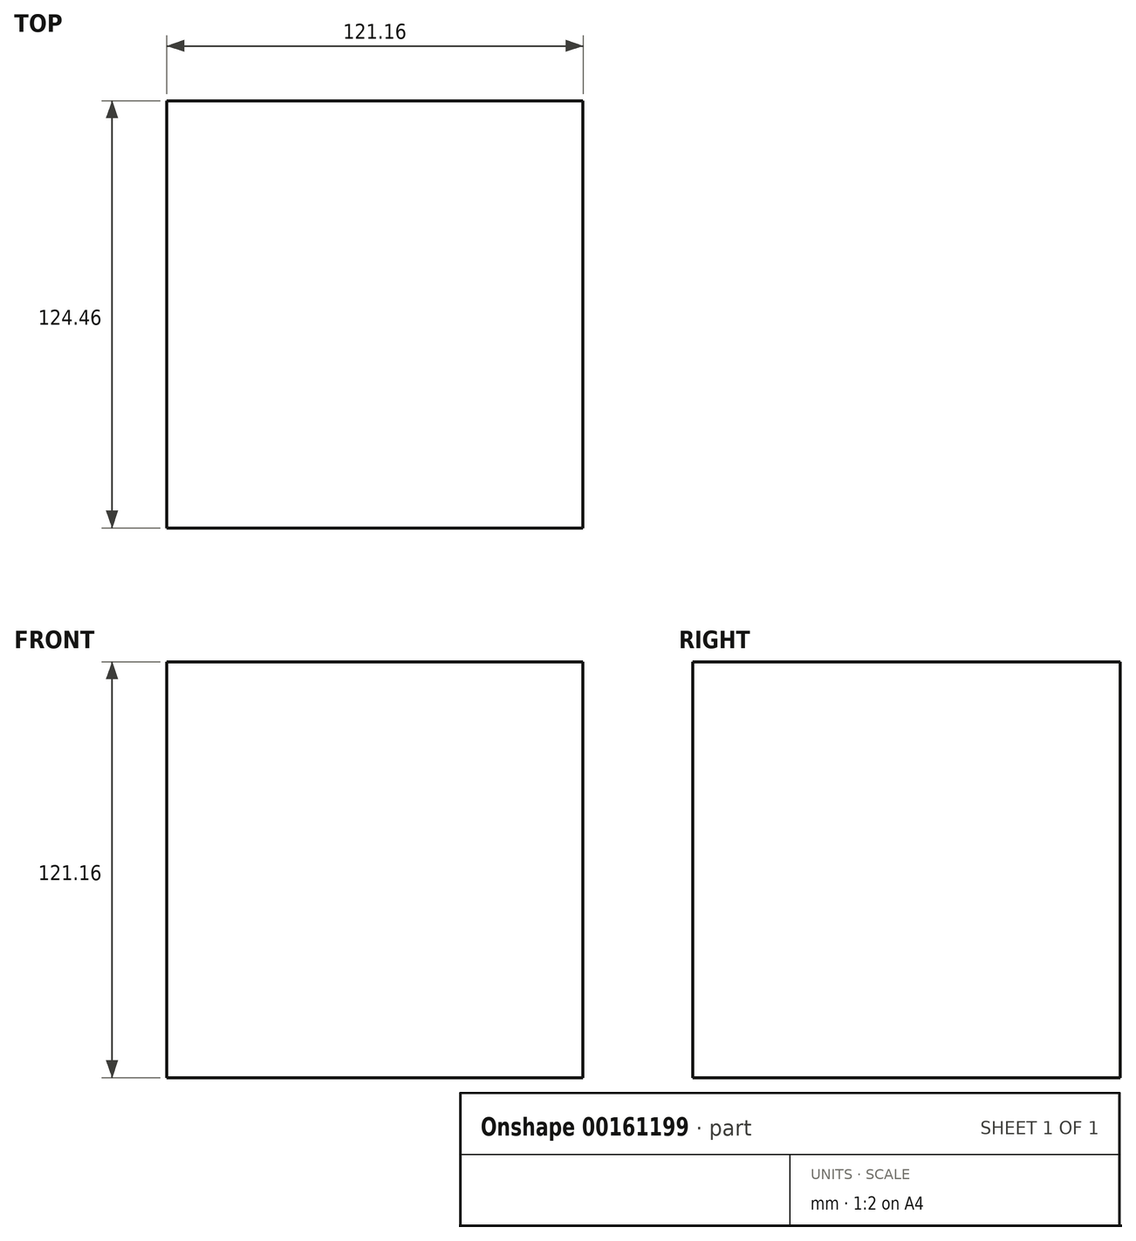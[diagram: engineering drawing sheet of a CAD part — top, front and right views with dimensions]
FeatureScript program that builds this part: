
annotation { "Feature Type Name" : "Feature", "Feature Type Description" : "" }
export const myFeature = defineFeature(function(context is Context, id is Id, definition is map)
    precondition{}
    {
        {
            var Q0;
            Q0=qCreatedBy(makeId("Front.planeOp"),FACE);
            var sketch = newSketch(context, id + "F0", { "sketchPlane" : qUnion([Q0])});
            skLineSegment(sketch, "E0.bottom", {"start": v(-62.62, 83.77) * mm, "end": v(58.54, 83.77) * mm});
            skLineSegment(sketch, "E0.top", {"start": v(-62.62, -37.39) * mm, "end": v(58.54, -37.39) * mm});
            skLineSegment(sketch, "E0.left", {"start": v(-62.62, 83.77) * mm, "end": v(-62.62, -37.39) * mm});
            skLineSegment(sketch, "E0.right", {"start": v(58.54, 83.77) * mm, "end": v(58.54, -37.39) * mm});
            skSolve(sketch);
        }
        {
            var Q0;
            Q0 = qSketchRegion(id + "F0", true);
            extrude(context, id + "F1", {"entities" : qUnion([Q0]), "depth" : 124.46 * mm});
        }
    });
